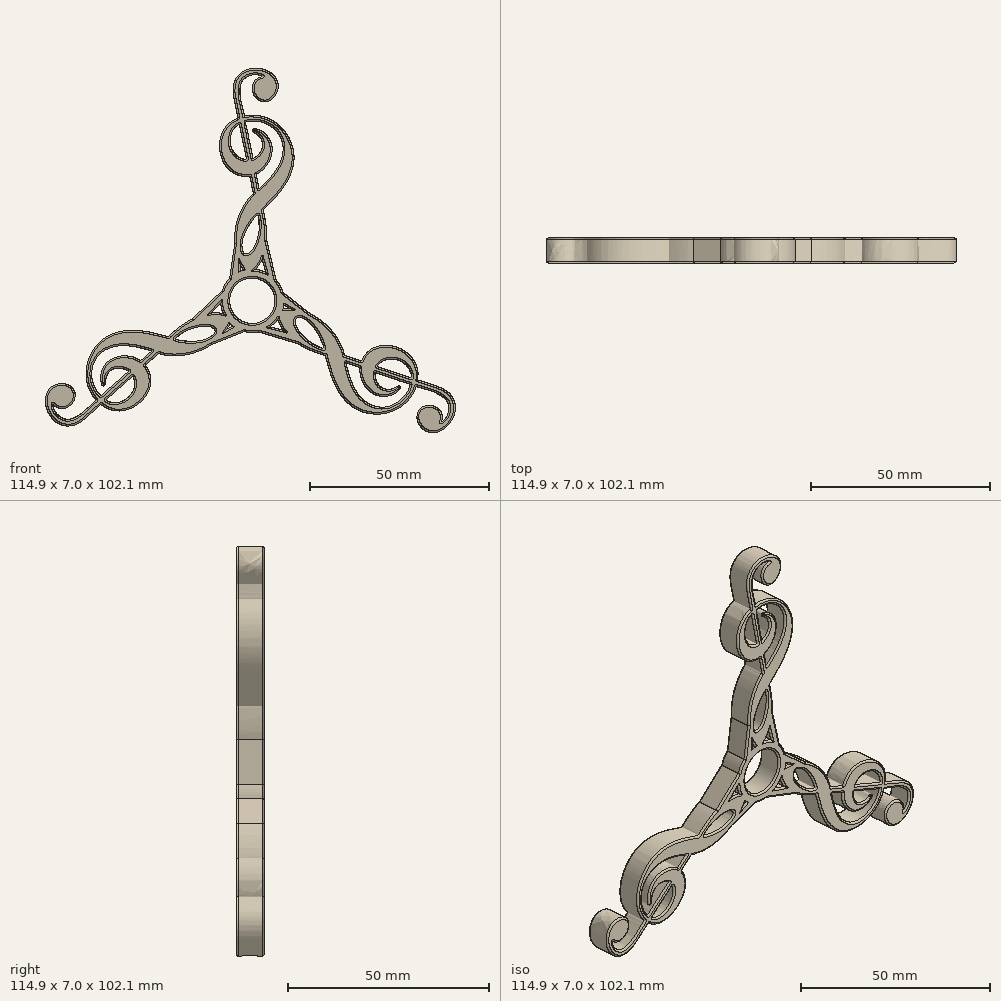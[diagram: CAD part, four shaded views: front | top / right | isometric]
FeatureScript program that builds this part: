
annotation { "Feature Type Name" : "Feature", "Feature Type Description" : "" }
export const myFeature = defineFeature(function(context is Context, id is Id, definition is map)
    precondition{}
    {
        {
            var Q0;
            Q0=qCreatedBy(makeId("Front.planeOp"),FACE);
            var sketch = newSketch(context, id + "F0", { "sketchPlane" : qUnion([Q0])});
            skCircle(sketch, "E0", {"center": v(0, 0) * mm, "radius": 8.9 * mm});
            skCircle(sketch, "E1", {"center": v(0, 0) * mm, "radius": 6.35 * mm});
            skFitSpline(sketch, "E2", {"points": [v(-1.93, 13.23) * mm, v(-2.12, 13.29) * mm, v(-2.33, 13.4) * mm, v(-2.5, 13.56) * mm, v(-2.65, 13.79) * mm, v(-2.75, 14) * mm, v(-2.82, 14.35) * mm, v(-2.86, 14.74) * mm, v(-2.9, 15.07) * mm, v(-2.92, 15.48) * mm, v(-2.9, 15.93) * mm, v(-2.83, 16.46) * mm, v(-2.71, 17.03) * mm, v(-2.62, 17.46) * mm, v(-2.47, 17.9) * mm, v(-2.3, 18.33) * mm, v(-2.08, 18.89) * mm, v(-1.85, 19.38) * mm, v(-1.64, 19.81) * mm, v(-1.45, 20.16) * mm, v(-1.24, 20.55) * mm, v(-0.98, 20.97) * mm, v(-0.65, 21.47) * mm, v(-0.35, 21.94) * mm, v(-0.13, 22.21) * mm, v(0.05, 22.43) * mm, v(0.43, 22.93) * mm, v(0.7, 23.27) * mm, v(1.05, 23.6) * mm, v(1.5, 24.03) * mm, v(1.56, 24.05) * mm, v(1.6, 23.91) * mm, v(1.7, 23.53) * mm, v(1.78, 23.1) * mm, v(1.9, 22.53) * mm, v(1.98, 21.92) * mm, v(2.02, 21.2) * mm, v(2, 20.73) * mm, v(1.92, 19.94) * mm, v(1.86, 19.45) * mm, v(1.8, 19.05) * mm, v(1.7, 18.53) * mm, v(1.6, 18.08) * mm, v(1.5, 17.69) * mm, v(1.4, 17.32) * mm, v(1.3, 16.95) * mm, v(1.13, 16.48) * mm, v(0.94, 15.99) * mm, v(0.83, 15.67) * mm, v(0.61, 15.2) * mm, v(0.41, 14.86) * mm, v(0.2, 14.47) * mm, v(0, 14.23) * mm, v(-0.23, 13.95) * mm, v(-0.62, 13.6) * mm, v(-0.84, 13.46) * mm, v(-1.24, 13.29) * mm, v(-1.73, 13.22) * mm, v(-1.93, 13.23) * mm]});
            skFitSpline(sketch, "E3", {"points": [v(3.03, 25.35) * mm, v(3.26, 25.58) * mm, v(3.57, 25.9) * mm, v(3.97, 26.3) * mm, v(4.28, 26.62) * mm, v(4.62, 26.97) * mm, v(4.97, 27.33) * mm, v(5.23, 27.6) * mm, v(5.54, 27.91) * mm, v(6.08, 28.51) * mm, v(6.55, 28.99) * mm, v(6.93, 29.4) * mm, v(7.2, 29.77) * mm, v(7.55, 30.2) * mm, v(7.97, 30.74) * mm, v(8.28, 31.12) * mm, v(8.6, 31.55) * mm, v(8.95, 32.06) * mm, v(9.28, 32.54) * mm, v(9.5, 32.92) * mm, v(9.7, 33.28) * mm, v(9.94, 33.68) * mm, v(10.13, 34.04) * mm, v(10.44, 34.74) * mm, v(10.71, 35.38) * mm, v(11, 36.15) * mm, v(11.17, 36.68) * mm, v(11.34, 37.26) * mm, v(11.46, 37.85) * mm, v(11.6, 38.65) * mm, v(11.65, 39.32) * mm, v(11.7, 39.8) * mm, v(11.7, 39.9) * mm, v(11.71, 39.98) * mm, v(11.71, 40.09) * mm, v(11.71, 40.17) * mm, v(11.7, 40.33) * mm, v(11.64, 40.9) * mm, v(11.6, 41.46) * mm, v(11.53, 41.96) * mm, v(11.47, 42.44) * mm, v(11.27, 43.08) * mm, v(11.11, 43.65) * mm, v(10.9, 44.27) * mm, v(10.7, 44.75) * mm, v(10.47, 45.26) * mm, v(10.17, 45.87) * mm, v(9.8, 46.48) * mm, v(9.63, 46.78) * mm, v(9.08, 47.53) * mm, v(8.7, 47.98) * mm, v(8.26, 48.5) * mm, v(7.76, 49) * mm, v(7, 49.64) * mm, v(6.43, 50.08) * mm, v(5.66, 50.54) * mm, v(4.7, 51.08) * mm, v(3.79, 51.42) * mm, v(3.1, 51.68) * mm, v(2.24, 51.87) * mm, v(1.44, 51.97) * mm, v(0.56, 52.05) * mm, v(-0.4, 52.09) * mm, v(-1.24, 52) * mm, v(-2.23, 51.83) * mm, v(-2.28, 52.08) * mm, v(-2.4, 52.6) * mm, v(-2.5, 52.96) * mm, v(-2.58, 53.4) * mm, v(-2.74, 53.93) * mm, v(-2.87, 54.6) * mm, v(-3.03, 55.27) * mm, v(-3.21, 56.04) * mm, v(-3.3, 56.52) * mm, v(-3.42, 57.2) * mm, v(-3.47, 57.91) * mm, v(-3.5, 58.45) * mm, v(-3.47, 59) * mm, v(-3.46, 59.68) * mm, v(-3.3, 60.4) * mm, v(-3.12, 60.96) * mm, v(-2.8, 61.58) * mm, v(-2.32, 62.12) * mm, v(-1.73, 62.6) * mm, v(-1.24, 62.9) * mm, v(-0.39, 63.21) * mm, v(0.25, 63.37) * mm, v(0.74, 63.42) * mm, v(1.36, 63.41) * mm, v(1.94, 63.3) * mm, v(2.61, 63.06) * mm, v(2.87, 62.86) * mm, v(2.76, 62.83) * mm, v(2.44, 62.75) * mm, v(1.94, 62.6) * mm, v(1.44, 62.3) * mm, v(1.06, 62.02) * mm, v(0.66, 61.56) * mm, v(0.31, 61) * mm, v(0.1, 60.4) * mm, v(0, 59.68) * mm, v(0.1, 58.76) * mm, v(0.2, 58.25) * mm, v(0.41, 57.76) * mm, v(0.66, 57.35) * mm, v(1.14, 56.8) * mm, v(1.78, 56.3) * mm, v(2.31, 56.04) * mm, v(2.74, 55.88) * mm, v(3.44, 55.78) * mm, v(4, 55.82) * mm, v(4.64, 56) * mm, v(5.25, 56.32) * mm, v(5.66, 56.6) * mm, v(6.07, 57.05) * mm, v(6.45, 57.52) * mm, v(6.7, 58) * mm, v(7.04, 58.8) * mm, v(7.18, 59.38) * mm, v(7.26, 60.08) * mm, v(7.14, 61.07) * mm, v(6.86, 61.9) * mm, v(6.47, 62.64) * mm, v(5.87, 63.37) * mm, v(5.34, 63.82) * mm, v(4.75, 64.2) * mm, v(4.17, 64.54) * mm, v(3.5, 64.83) * mm, v(2.95, 64.97) * mm, v(2.22, 65.15) * mm, v(1.71, 65.17) * mm, v(0.85, 65.2) * mm, v(0.2, 65.17) * mm, v(-0.12, 65.13) * mm, v(-0.62, 65.05) * mm, v(-1.1, 64.9) * mm, v(-1.73, 64.7) * mm, v(-2.27, 64.44) * mm, v(-2.7, 64.17) * mm, v(-3.2, 63.86) * mm, v(-3.52, 63.55) * mm, v(-3.92, 63.16) * mm, v(-4.32, 62.64) * mm, v(-4.65, 62.11) * mm, v(-4.83, 61.72) * mm, v(-5.14, 61.02) * mm, v(-5.3, 60.31) * mm, v(-5.36, 59.49) * mm, v(-5.4, 58.77) * mm, v(-5.32, 57.95) * mm, v(-5.21, 57.1) * mm, v(-5.07, 56.35) * mm, v(-4.91, 55.53) * mm, v(-4.68, 54.45) * mm, v(-4.45, 53.4) * mm, v(-4.28, 52.6) * mm, v(-4.14, 51.83) * mm, v(-4, 51.2) * mm, v(-4.1, 51.16) * mm, v(-4.52, 50.98) * mm, v(-5.02, 50.71) * mm, v(-5.52, 50.43) * mm, v(-6.1, 50.07) * mm, v(-6.53, 49.68) * mm, v(-6.99, 49.2) * mm, v(-7.44, 48.76) * mm, v(-7.78, 48.2) * mm, v(-8.19, 47.54) * mm, v(-8.52, 46.8) * mm, v(-8.78, 46.09) * mm, v(-9.03, 45.2) * mm, v(-9.16, 44.19) * mm, v(-9.18, 43.91) * mm, v(-9.18, 42.81) * mm, v(-9.11, 42.26) * mm, v(-8.97, 41.35) * mm, v(-8.86, 40.86) * mm, v(-8.65, 40.2) * mm, v(-8.46, 39.67) * mm, v(-8.18, 39.1) * mm, v(-7.94, 38.63) * mm, v(-7.5, 37.96) * mm, v(-7.18, 37.52) * mm, v(-6.5, 36.8) * mm, v(-5.77, 36.19) * mm, v(-4.5, 35.47) * mm, v(-3.5, 35.14) * mm, v(-2.66, 34.95) * mm, v(-1.9, 34.9) * mm, v(-1.24, 34.94) * mm, v(-0.74, 34.99) * mm, v(-0.7, 34.82) * mm, v(-0.56, 34.25) * mm, v(-0.43, 33.63) * mm, v(-0.23, 32.87) * mm, v(-0.14, 32.07) * mm, v(0, 31.53) * mm, v(0.12, 30.93) * mm, v(0.25, 30.29) * mm, v(0.3, 30) * mm, v(0.14, 29.87) * mm, v(-0.16, 29.56) * mm, v(-0.62, 29.14) * mm, v(-1.17, 28.38) * mm, v(-1.62, 27.8) * mm, v(-1.96, 27.34) * mm, v(-2.4, 26.65) * mm, v(-2.72, 26.06) * mm, v(-3.03, 25.54) * mm, v(-3.3, 24.92) * mm, v(-3.66, 24.06) * mm, v(-4, 23.15) * mm, v(-4.34, 22.05) * mm, v(-4.56, 21.26) * mm, v(-4.62, 20.6) * mm, v(-4.74, 20) * mm, v(-4.87, 19.24) * mm, v(-4.96, 18.35) * mm, v(-4.98, 17.54) * mm, v(-4.98, 16.57) * mm, v(-4.94, 16) * mm, v(-4.86, 15.1) * mm, v(-4.74, 14.23) * mm, v(-4.56, 13.39) * mm, v(-4.34, 12.54) * mm, v(-4.07, 11.7) * mm, v(-3.72, 10.86) * mm, v(-3.39, 10.15) * mm, v(-2.91, 9.3) * mm, v(-2.55, 8.71) * mm, v(-2.31, 8.4) * mm, v(-1.83, 7.88) * mm, v(-1.24, 7.63) * mm, v(-0.57, 7.71) * mm, v(-0.06, 8) * mm, v(0.55, 8.43) * mm, v(1, 8.83) * mm, v(1.53, 9.45) * mm, v(2.05, 10.24) * mm, v(2.45, 10.87) * mm, v(2.77, 11.61) * mm, v(3.04, 12.33) * mm, v(3.25, 13) * mm, v(3.45, 13.72) * mm, v(3.63, 14.47) * mm, v(3.75, 15.2) * mm, v(3.9, 16.13) * mm, v(4, 17.06) * mm, v(4.02, 17.73) * mm, v(4.04, 18.52) * mm, v(4.02, 19.14) * mm, v(3.96, 20.02) * mm, v(3.87, 20.8) * mm, v(3.73, 21.93) * mm, v(3.62, 22.63) * mm, v(3.44, 23.59) * mm, v(3.28, 24.32) * mm, v(3.12, 25.04) * mm, v(3.03, 25.35) * mm]});
            skFitSpline(sketch, "E4", {"points": [v(-1.59, 39.6) * mm, v(-1.96, 39.62) * mm, v(-2.54, 39.73) * mm, v(-3.34, 40.01) * mm, v(-3.9, 40.32) * mm, v(-4.68, 40.95) * mm, v(-5.02, 41.36) * mm, v(-5.44, 42.03) * mm, v(-5.77, 42.6) * mm, v(-5.95, 43.12) * mm, v(-6.12, 43.71) * mm, v(-6.2, 44.3) * mm, v(-6.23, 44.83) * mm, v(-6.17, 45.37) * mm, v(-6.07, 46) * mm, v(-5.92, 46.57) * mm, v(-5.77, 47.16) * mm, v(-5.54, 47.54) * mm, v(-5.07, 48.3) * mm, v(-4.68, 48.7) * mm, v(-4.37, 48.97) * mm, v(-3.95, 49.28) * mm, v(-3.6, 49.44) * mm, v(-3.57, 49.35) * mm, v(-3.56, 49.2) * mm, v(-3.45, 48.7) * mm, v(-3.32, 48.15) * mm, v(-3.18, 47.43) * mm, v(-3.07, 46.89) * mm, v(-2.97, 46.3) * mm, v(-2.71, 45.2) * mm, v(-2.56, 44.33) * mm, v(-2.4, 43.55) * mm, v(-2.22, 42.6) * mm, v(-2.1, 41.9) * mm, v(-1.94, 41.3) * mm, v(-1.83, 40.71) * mm, v(-1.67, 40.03) * mm, v(-1.6, 39.72) * mm, v(-1.59, 39.6) * mm]});
            skFitSpline(sketch, "E5", {"points": [v(0.2, 39.83) * mm, v(0.53, 40) * mm, v(0.99, 40.29) * mm, v(1.5, 40.71) * mm, v(1.97, 41.18) * mm, v(2.31, 41.65) * mm, v(2.54, 42.12) * mm, v(2.8, 42.6) * mm, v(2.88, 43.2) * mm, v(2.92, 43.66) * mm, v(2.88, 44.19) * mm, v(2.68, 44.82) * mm, v(2.5, 45.3) * mm, v(2.13, 45.9) * mm, v(1.73, 46.37) * mm, v(1.3, 46.67) * mm, v(0.66, 47.03) * mm, v(0.41, 47.13) * mm, v(0.11, 47.46) * mm, v(0.07, 47.79) * mm, v(0.2, 48.08) * mm, v(0.41, 48.21) * mm, v(0.7, 48.3) * mm, v(0.93, 48.3) * mm, v(1.47, 48.12) * mm, v(1.92, 47.94) * mm, v(2.43, 47.67) * mm, v(3.12, 47.26) * mm, v(3.57, 46.8) * mm, v(3.97, 46.44) * mm, v(4.35, 45.95) * mm, v(4.67, 45.5) * mm, v(4.93, 45.02) * mm, v(5.15, 44.53) * mm, v(5.27, 44.19) * mm, v(5.43, 43.57) * mm, v(5.55, 42.95) * mm, v(5.58, 42.48) * mm, v(5.55, 41.98) * mm, v(5.47, 41.36) * mm, v(5.37, 40.84) * mm, v(5.14, 40) * mm, v(4.95, 39.45) * mm, v(4.65, 38.83) * mm, v(4.24, 38.18) * mm, v(3.71, 37.5) * mm, v(3.39, 37.1) * mm, v(3.03, 36.7) * mm, v(2.43, 36.26) * mm, v(1.81, 35.82) * mm, v(1.36, 35.6) * mm, v(1.15, 35.48) * mm, v(1.08, 35.45) * mm, v(1.08, 35.33) * mm, v(1.22, 34.71) * mm, v(1.3, 34.28) * mm, v(1.4, 33.68) * mm, v(1.52, 33.17) * mm, v(1.63, 32.6) * mm, v(1.72, 32.13) * mm, v(1.8, 31.65) * mm, v(1.92, 31.4) * mm, v(2.07, 31.57) * mm, v(2.45, 31.93) * mm, v(2.89, 32.33) * mm, v(3.38, 32.76) * mm, v(3.68, 33.12) * mm, v(4.05, 33.48) * mm, v(4.41, 33.88) * mm, v(4.88, 34.38) * mm, v(5.26, 34.76) * mm, v(5.6, 35.24) * mm, v(5.94, 35.67) * mm, v(6.33, 36.19) * mm, v(6.73, 36.68) * mm, v(6.95, 37.15) * mm, v(7.23, 37.6) * mm, v(7.55, 38.21) * mm, v(7.8, 38.67) * mm, v(7.98, 39.2) * mm, v(8.15, 39.63) * mm, v(8.32, 40.26) * mm, v(8.46, 40.94) * mm, v(8.54, 41.59) * mm, v(8.6, 42.1) * mm, v(8.64, 42.6) * mm, v(8.6, 43.2) * mm, v(8.55, 43.72) * mm, v(8.45, 44.19) * mm, v(8.32, 44.75) * mm, v(8.07, 45.47) * mm, v(7.87, 45.87) * mm, v(7.58, 46.45) * mm, v(7.29, 46.87) * mm, v(6.86, 47.54) * mm, v(6.3, 48.1) * mm, v(5.83, 48.5) * mm, v(5.32, 48.86) * mm, v(4.7, 49.28) * mm, v(4.16, 49.55) * mm, v(3.44, 49.87) * mm, v(2.83, 50.05) * mm, v(2.16, 50.24) * mm, v(1.3, 50.35) * mm, v(0.67, 50.42) * mm, v(0, 50.42) * mm, v(-0.53, 50.33) * mm, v(-1.1, 50.23) * mm, v(-1.73, 50.1) * mm, v(-1.83, 50) * mm, v(-1.83, 49.86) * mm, v(-1.83, 49.47) * mm, v(-1.66, 48.96) * mm, v(-1.55, 48.34) * mm, v(-1.44, 47.79) * mm, v(-1.24, 47.17) * mm, v(-1.14, 46.4) * mm, v(-0.95, 45.44) * mm, v(-0.73, 44.19) * mm, v(-0.55, 43.33) * mm, v(-0.4, 42.6) * mm, v(-0.23, 41.77) * mm, v(0, 40.8) * mm, v(0.08, 40.17) * mm, v(0.2, 39.83) * mm]});
            skPoint(sketch, "E6", {"position": v(-6.36, 6.21) * mm});
            skPoint(sketch, "E7", {"position": v(6.62, 5.93) * mm});
            skPoint(sketch, "E8", {"position": v(3.75, 8.06) * mm});
            skLineSegment(sketch, "E9", {"start": v(-6.36, 6.21) * mm, "end": v(-4.94, 16) * mm});
            skLineSegment(sketch, "E10", {"start": v(-3.39, 10.15) * mm, "end": v(-3.39, 8.22) * mm});
            skLineSegment(sketch, "E11", {"start": v(6.62, 5.93) * mm, "end": v(4, 17.06) * mm});
            skLineSegment(sketch, "E12", {"start": v(3.75, 8.06) * mm, "end": v(2.77, 11.61) * mm});
            skSolve(sketch);
        }
        {
            var Q0;
            {var subQ0=sQuery(id+"F0.wireOp",EDGE,"E9");Q0=makeQuery(id+"F0.imprint","IMPRINT",FACE,{"disambiguationData":[TD([[makeQuery(id+"F0.imprint","IMPRINT",EDGE,{"derivedFrom":subQ0}),-1.0]])]});}
            var Q1;
            Q1=makeQuery(id+"F0.imprint","IMPRINT",FACE,{"disambiguationData":[TD([[makeQuery(id+"F0.imprint","IMPRINT",EDGE,{"derivedFrom":sQuery(id+"F0.wireOp",EDGE,"E2")}),1.0]])]});
            var Q2;
            {var subQ0=sQuery(id+"F0.wireOp",EDGE,"E11");Q2=makeQuery(id+"F0.imprint","IMPRINT",FACE,{"disambiguationData":[TD([[makeQuery(id+"F0.imprint","IMPRINT",EDGE,{"derivedFrom":subQ0}),1.0]])]});}
            var Q3;
            {var subQ0=sQuery(id+"F0.wireOp",EDGE,"E3");var subQ1=sQuery(id+"F0.wireOp",EDGE,"E0");var subQ2=makeQuery(id+"F0.imprint","INTERSECT",VERTEX,{"disambiguationData":[OD(0.0)],"derivedFrom":[subQ1,subQ0]});Q3=makeQuery(id+"F0.imprint","IMPRINT",FACE,{"disambiguationData":[TD([[makeQuery(id+"F0.imprint","IMPRINT",EDGE,{"disambiguationData":[TD([[subQ2,-1.0]])],"derivedFrom":subQ1}),1.0]])]});}
            var Q4;
            Q4=makeQuery(id+"F0.imprint","IMPRINT",FACE,{"disambiguationData":[TD([[makeQuery(id+"F0.imprint","IMPRINT",EDGE,{"derivedFrom":sQuery(id+"F0.wireOp",EDGE,"E1")}),-1.0]])]});
            extrude(context, id + "F1", {"entities" : qUnion([Q0, Q1, Q2, Q3, Q4]), "depth" : 7 * mm, "offsetDistance" : 25.4 * mm});
        }
        {
            var Q0;
            Q0=makeQuery(id+"F1.opExtrude","CAP_EDGE",EDGE,{"disambiguationData":[OSD([sQuery(id+"F0.wireOp",EDGE,"E5")])],"isStart":false});
            var Q1;
            Q1=makeQuery(id+"F1.opExtrude","CAP_EDGE",EDGE,{"disambiguationData":[OSD([sQuery(id+"F0.wireOp",EDGE,"E4")])],"isStart":false});
            var Q2;
            Q2=makeQuery(id+"F1.opExtrude","CAP_EDGE",EDGE,{"disambiguationData":[OSD([sQuery(id+"F0.wireOp",EDGE,"E2")])],"isStart":false});
            var Q3;
            {var subQ0=sQuery(id+"F0.wireOp",EDGE,"E3");Q3=makeQuery(id+"F1.opExtrude","CAP_EDGE",EDGE,{"disambiguationData":[OSD([subQ0]),TDD([makeQuery(id+"F0.imprint","IMPRINT",EDGE,{"disambiguationData":[TD([[makeQuery(id+"F0.imprint","INTERSECT",VERTEX,{"derivedFrom":[subQ0,sQuery(id+"F0.wireOp",EDGE,"E10")]}),-1.0]])],"derivedFrom":subQ0})])],"isStart":false});}
            var Q4;
            Q4=makeQuery(id+"F1.opExtrude","CAP_EDGE",EDGE,{"disambiguationData":[OSD([sQuery(id+"F0.wireOp",EDGE,"E10")])],"isStart":false});
            var Q5;
            {var subQ0=sQuery(id+"F0.wireOp",EDGE,"E0");Q5=makeQuery(id+"F1.opExtrude","CAP_EDGE",EDGE,{"disambiguationData":[OSD([subQ0]),TDD([makeQuery(id+"F0.imprint","IMPRINT",EDGE,{"disambiguationData":[TD([[makeQuery(id+"F0.imprint","INTERSECT",VERTEX,{"derivedFrom":[subQ0,sQuery(id+"F0.wireOp",EDGE,"E12")]}),-1.0]])],"derivedFrom":subQ0})])],"isStart":false});}
            var Q6;
            {var subQ0=sQuery(id+"F0.wireOp",EDGE,"E3");Q6=makeQuery(id+"F1.opExtrude","CAP_EDGE",EDGE,{"disambiguationData":[OSD([subQ0]),TDD([makeQuery(id+"F0.imprint","IMPRINT",EDGE,{"disambiguationData":[TD([[makeQuery(id+"F0.imprint","INTERSECT",VERTEX,{"derivedFrom":[subQ0,sQuery(id+"F0.wireOp",EDGE,"E12")]}),1.0]])],"derivedFrom":subQ0})])],"isStart":false});}
            var Q7;
            Q7=makeQuery(id+"F1.opExtrude","CAP_EDGE",EDGE,{"disambiguationData":[OSD([sQuery(id+"F0.wireOp",EDGE,"E12")])],"isStart":false});
            var Q8;
            Q8=makeQuery(id+"F1.opExtrude","CAP_EDGE",EDGE,{"disambiguationData":[OSD([sQuery(id+"F0.wireOp",EDGE,"E1")])],"isStart":false});
            var Q9;
            {var subQ0=sQuery(id+"F0.wireOp",EDGE,"E0");Q9=makeQuery(id+"F1.opExtrude","CAP_EDGE",EDGE,{"disambiguationData":[OSD([subQ0]),TDD([makeQuery(id+"F0.imprint","IMPRINT",EDGE,{"disambiguationData":[TD([[makeQuery(id+"F0.imprint","INTERSECT",VERTEX,{"derivedFrom":[subQ0,sQuery(id+"F0.wireOp",EDGE,"E9")]}),-1.0]])],"derivedFrom":subQ0})])],"isStart":false});}
            var Q10;
            Q10=makeQuery(id+"F1.opExtrude","CAP_EDGE",EDGE,{"disambiguationData":[OSD([sQuery(id+"F0.wireOp",EDGE,"E11")])],"isStart":false});
            var Q11;
            Q11=makeQuery(id+"F1.opExtrude","CAP_EDGE",EDGE,{"disambiguationData":[OSD([sQuery(id+"F0.wireOp",EDGE,"E9")])],"isStart":false});
            var Q12;
            {var subQ0=sQuery(id+"F0.wireOp",EDGE,"E3");Q12=makeQuery(id+"F1.opExtrude","CAP_EDGE",EDGE,{"disambiguationData":[OSD([subQ0]),TDD([makeQuery(id+"F0.imprint","IMPRINT",EDGE,{"disambiguationData":[TD([[makeQuery(id+"F0.imprint","INTERSECT",VERTEX,{"derivedFrom":[subQ0,sQuery(id+"F0.wireOp",EDGE,"E9")]}),1.0]])],"derivedFrom":subQ0})])],"isStart":false});}
            var Q13;
            Q13=makeQuery(id+"F1.opExtrude","CAP_EDGE",EDGE,{"disambiguationData":[OSD([sQuery(id+"F0.wireOp",EDGE,"E1")])],"isStart":true});
            var Q14;
            Q14=makeQuery(id+"F1.opExtrude","CAP_EDGE",EDGE,{"disambiguationData":[OSD([sQuery(id+"F0.wireOp",EDGE,"E10")])],"isStart":true});
            var Q15;
            {var subQ0=sQuery(id+"F0.wireOp",EDGE,"E0");Q15=makeQuery(id+"F1.opExtrude","CAP_EDGE",EDGE,{"disambiguationData":[OSD([subQ0]),TDD([makeQuery(id+"F0.imprint","IMPRINT",EDGE,{"disambiguationData":[TD([[makeQuery(id+"F0.imprint","INTERSECT",VERTEX,{"derivedFrom":[subQ0,sQuery(id+"F0.wireOp",EDGE,"E10")]}),1.0]])],"derivedFrom":subQ0})])],"isStart":true});}
            var Q16;
            {var subQ0=sQuery(id+"F0.wireOp",EDGE,"E3");Q16=makeQuery(id+"F1.opExtrude","CAP_EDGE",EDGE,{"disambiguationData":[OSD([subQ0]),TDD([makeQuery(id+"F0.imprint","IMPRINT",EDGE,{"disambiguationData":[TD([[makeQuery(id+"F0.imprint","INTERSECT",VERTEX,{"derivedFrom":[subQ0,sQuery(id+"F0.wireOp",EDGE,"E10")]}),-1.0]])],"derivedFrom":subQ0})])],"isStart":true});}
            var Q17;
            {var subQ0=sQuery(id+"F0.wireOp",EDGE,"E3");Q17=makeQuery(id+"F1.opExtrude","CAP_EDGE",EDGE,{"disambiguationData":[OSD([subQ0]),TDD([makeQuery(id+"F0.imprint","IMPRINT",EDGE,{"disambiguationData":[TD([[makeQuery(id+"F0.imprint","INTERSECT",VERTEX,{"derivedFrom":[subQ0,sQuery(id+"F0.wireOp",EDGE,"E12")]}),1.0]])],"derivedFrom":subQ0})])],"isStart":true});}
            var Q18;
            {var subQ0=sQuery(id+"F0.wireOp",EDGE,"E0");Q18=makeQuery(id+"F1.opExtrude","CAP_EDGE",EDGE,{"disambiguationData":[OSD([subQ0]),TDD([makeQuery(id+"F0.imprint","IMPRINT",EDGE,{"disambiguationData":[TD([[makeQuery(id+"F0.imprint","INTERSECT",VERTEX,{"derivedFrom":[subQ0,sQuery(id+"F0.wireOp",EDGE,"E12")]}),-1.0]])],"derivedFrom":subQ0})])],"isStart":true});}
            var Q19;
            Q19=makeQuery(id+"F1.opExtrude","CAP_EDGE",EDGE,{"disambiguationData":[OSD([sQuery(id+"F0.wireOp",EDGE,"E12")])],"isStart":true});
            var Q20;
            {var subQ0=sQuery(id+"F0.wireOp",EDGE,"E0");Q20=makeQuery(id+"F1.opExtrude","CAP_EDGE",EDGE,{"disambiguationData":[OSD([subQ0]),TDD([makeQuery(id+"F0.imprint","IMPRINT",EDGE,{"disambiguationData":[TD([[makeQuery(id+"F0.imprint","INTERSECT",VERTEX,{"derivedFrom":[subQ0,sQuery(id+"F0.wireOp",EDGE,"E9")]}),-1.0]])],"derivedFrom":subQ0})])],"isStart":true});}
            var Q21;
            Q21=makeQuery(id+"F1.opExtrude","CAP_EDGE",EDGE,{"disambiguationData":[OSD([sQuery(id+"F0.wireOp",EDGE,"E2")])],"isStart":true});
            var Q22;
            Q22=makeQuery(id+"F1.opExtrude","CAP_EDGE",EDGE,{"disambiguationData":[OSD([sQuery(id+"F0.wireOp",EDGE,"E5")])],"isStart":true});
            var Q23;
            Q23=makeQuery(id+"F1.opExtrude","CAP_EDGE",EDGE,{"disambiguationData":[OSD([sQuery(id+"F0.wireOp",EDGE,"E4")])],"isStart":true});
            var Q24;
            Q24=makeQuery(id+"F1.opExtrude","CAP_EDGE",EDGE,{"disambiguationData":[OSD([sQuery(id+"F0.wireOp",EDGE,"E9")])],"isStart":true});
            var Q25;
            Q25=makeQuery(id+"F1.opExtrude","CAP_FACE",FACE,{"disambiguationData":[OSD([sQuery(id+"F0.wireOp",EDGE,"E0"),sQuery(id+"F0.wireOp",EDGE,"E1"),sQuery(id+"F0.wireOp",EDGE,"E2"),sQuery(id+"F0.wireOp",EDGE,"E3"),sQuery(id+"F0.wireOp",EDGE,"E4"),sQuery(id+"F0.wireOp",EDGE,"E5"),sQuery(id+"F0.wireOp",EDGE,"E9"),sQuery(id+"F0.wireOp",EDGE,"E10"),sQuery(id+"F0.wireOp",EDGE,"E11"),sQuery(id+"F0.wireOp",EDGE,"E12")])],"isStart":true});
            fillet(context, id + "F2", {"entities" : qUnion([Q0, Q1, Q2, Q3, Q4, Q5, Q6, Q7, Q8, Q9, Q10, Q11, Q12, Q13, Q14, Q15, Q16, Q17, Q18, Q19, Q20, Q21, Q22, Q23, Q24, Q25]), "radius" : 0.5 * mm, "tangentPropagation" : true, "allowEdgeOverflow" : false});
        }
        {
            var Q0;
            Q0=makeQuery(id+"F1.opExtrude","SWEPT_BODY",BODY,{"disambiguationData":[OSD([sQuery(id+"F0.wireOp",EDGE,"E0"),sQuery(id+"F0.wireOp",EDGE,"E1"),sQuery(id+"F0.wireOp",EDGE,"E2"),sQuery(id+"F0.wireOp",EDGE,"E3"),sQuery(id+"F0.wireOp",EDGE,"E4"),sQuery(id+"F0.wireOp",EDGE,"E5"),sQuery(id+"F0.wireOp",EDGE,"E9"),sQuery(id+"F0.wireOp",EDGE,"E10"),sQuery(id+"F0.wireOp",EDGE,"E11"),sQuery(id+"F0.wireOp",EDGE,"E12")])]});
            var Q1;
            Q1=makeQuery(id+"F1.opExtrude","SWEPT_FACE",FACE,{"disambiguationData":[OSD([sQuery(id+"F0.wireOp",EDGE,"E1")])]});
            circularPattern(context, id + "F3", {"operationType" : NewBodyOperationType.ADD, "entities" : qUnion([Q0]), "axis" : qUnion([Q1]), "angle" : 360 * degree, "instanceCount" : 3, "equalSpace" : true});
        }
    });
